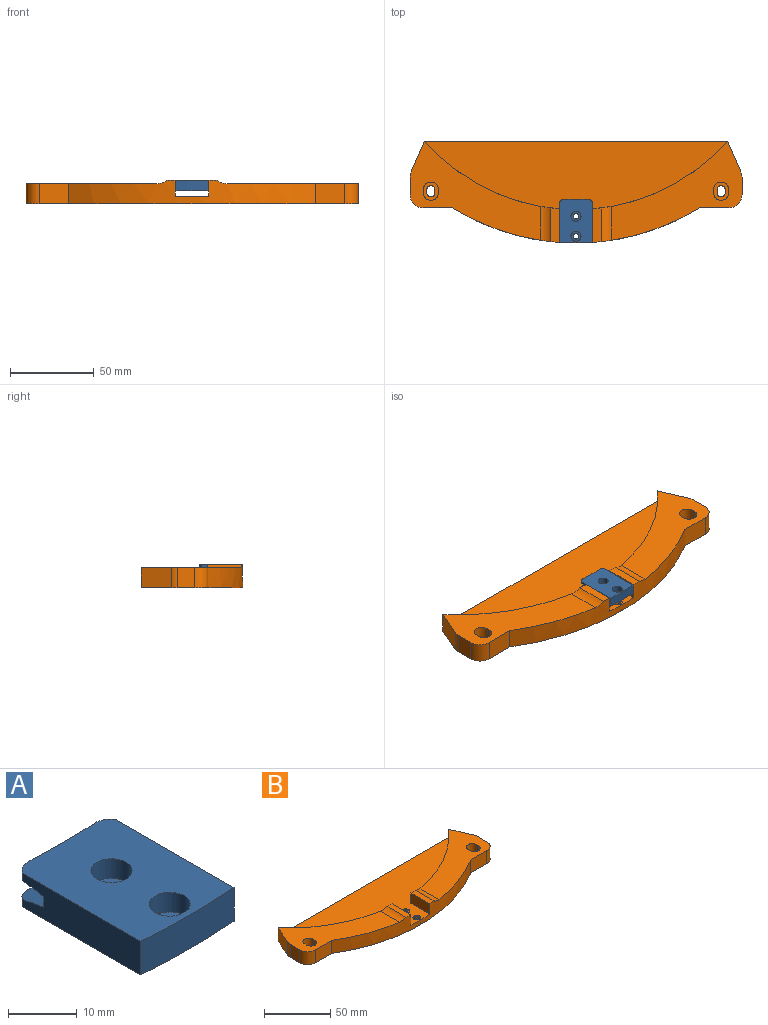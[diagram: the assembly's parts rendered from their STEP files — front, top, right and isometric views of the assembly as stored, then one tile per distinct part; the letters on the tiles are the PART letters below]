
ASSEMBLY  parts=2 mates=1
PART A: 24 faces, bbox 19.9x26.4x6 mm
  f0: cylinder r=1.7mm len=3.4mm, axis (0,0,1), area 21.4mm2, adj f10,f23
  f1: cylinder r=1.7mm len=3.4mm, axis (0,0,1), area 21.4mm2, adj f11,f21
  f2: plane 26.21x19.2mm, normal (0,0,1), area 440.4mm2, adj f7,f9,f12,f13,f14,f15,f18,f19
  f3: plane 26.21x19.2mm, normal (0,0,-1), area 440.4mm2, adj f7,f8,f16,f17,f18,f19,f20,f22
  f4: cylinder r=121mm len=19.2mm, axis (0,0,-1), area 36.1mm2, adj f5,f6,f18,f19
  f5: cone r=114.99mm half-angle=80deg, axis (0,0,1), area 114.3mm2, adj f4,f8,f16,f17,f18,f19
  f6: cone r=121mm half-angle=80deg, axis (0,0,-1), area 114.3mm2, adj f4,f9,f14,f15,f18,f19
  f7: cylinder r=141mm len=19.2mm, axis (0,0,-1), area 115.3mm2, adj f2,f3,f18,f19
  f8: cylinder r=115mm len=13.64mm, axis (0,0,-1), area 13.7mm2, adj f3,f5,f16,f17
  f9: cylinder r=115mm len=13.64mm, axis (0,0,-1), area 13.7mm2, adj f2,f6,f14,f15
  f10: plane 6x6mm, normal (0,0,1), area 19.2mm2, adj f0,f13
  f11: plane 6x6mm, normal (0,0,1), area 19.2mm2, adj f1,f12
  f12: cylinder r=3mm len=6mm, axis (0,0,1), area 66mm2, adj f2,f11
  f13: cylinder r=3mm len=6mm, axis (0,0,1), area 66mm2, adj f2,f10
  f14: cylinder r=3mm len=2.78mm, axis (0,0,-1), area 3.8mm2, adj f2,f6,f9,f18
  f15: cylinder r=3mm len=2.78mm, axis (0,0,-1), area 3.8mm2, adj f2,f6,f9,f19
  f16: cylinder r=3mm len=2.78mm, axis (0,0,-1), area 3.8mm2, adj f3,f5,f8,f18
  f17: cylinder r=3mm len=2.78mm, axis (0,0,-1), area 3.8mm2, adj f3,f5,f8,f19
  f18: plane 24.39x6.01mm, normal (1,0,0), area 134.9mm2, adj f2,f3,f4,f5,f6,f7,f14,f16
  f19: plane 24.39x6.01mm, normal (-1,0,0), area 134.9mm2, adj f2,f3,f4,f5,f6,f7,f15,f17
  f20: cylinder r=3mm len=6mm, axis (0,0,-1), area 9.4mm2, adj f3,f21
  f21: plane 6x6mm, normal (0,0,-1), area 19.2mm2, adj f1,f20
  f22: cylinder r=3mm len=6mm, axis (0,0,-1), area 9.4mm2, adj f3,f23
  f23: plane 6x6mm, normal (0,0,-1), area 19.2mm2, adj f0,f22
PART B: 84 faces, bbox 198.8x61x14 mm
  f0: plane 0.61x0.17mm, normal (0,0,-1), area 0mm2, adj f45,f70,f71
  f1: plane 0.52x0.3mm, normal (0,0,-1), area 0mm2, adj f45,f68,f70
  f2: plane 0.52x0.3mm, normal (0,0,-1), area 0mm2, adj f45,f66,f68
  f3: plane 0.61x0.17mm, normal (0,0,-1), area 0mm2, adj f45,f66,f67
  f4: plane 0.52x0.3mm, normal (0,0,-1), area 0mm2, adj f45,f69,f71
  f5: plane 0.52x0.3mm, normal (0,0,-1), area 0mm2, adj f44,f63,f65
  f6: plane 0.61x0.17mm, normal (0,0,-1), area 0mm2, adj f44,f61,f63
  f7: plane 0.52x0.3mm, normal (0,0,-1), area 0mm2, adj f44,f60,f61
  f8: plane 0.52x0.3mm, normal (0,0,-1), area 0mm2, adj f44,f60,f62
  f9: plane 0.52x0.3mm, normal (0,0,-1), area 0mm2, adj f44,f64,f65
  f10: plane 198.81x61mm, normal (0,0,-1), area 9740.1mm2, adj f16,f17,f18,f19,f20,f21,f22,f23
  f11: plane 78.4x59.43mm, normal (0,0,1), area 1845.7mm2, adj f17,f18,f19,f20,f33,f40,f41,f42
  f12: plane 78.4x59.43mm, normal (0,0,1), area 1845.7mm2, adj f20,f21,f22,f23,f34,f36,f37,f38
  f13: plane 181.56x61mm, normal (0,0,1), area 5503.4mm2, adj f16,f20,f32,f33,f34,f35,f72,f74
  f14: plane 11x9mm, normal (0,0,1), area 53.9mm2, adj f28,f29,f30,f31,f36,f37,f38,f39
  f15: plane 11x9mm, normal (0,0,1), area 53.9mm2, adj f24,f25,f26,f27,f40,f41,f42,f43
  f16: plane 181.56x4.5mm, normal (0,1,0), area 817mm2, adj f10,f13,f17,f23
  f17: plane 18.48x12mm, normal (-0.92,0.4,0), area 241.5mm2, adj f10,f11,f16,f33,f76
  f18: plane 12x10.35mm, normal (-1,0,0), area 124.2mm2, adj f10,f11,f76,f79
  f19: plane 17.37x12mm, normal (0,-1,0), area 208.4mm2, adj f10,f11,f20,f79
  f20: cylinder r=141mm len=148.07mm, axis (0,0,-1), area 1748.3mm2, adj f10,f11,f12,f13,f19,f21,f32,f35
  f21: plane 17.37x12mm, normal (0,-1,0), area 208.4mm2, adj f10,f12,f20,f78
  f22: plane 12x10.35mm, normal (1,0,0), area 124.2mm2, adj f10,f12,f77,f78
  f23: plane 18.48x12mm, normal (0.92,0.4,0), area 241.5mm2, adj f10,f12,f16,f34,f77
  f24: cylinder r=2.4mm len=4.8mm, axis (0,0,-1), area 33.9mm2, adj f10,f15,f25,f27
  f25: plane 4.5x2mm, normal (1,0,0), area 9mm2, adj f10,f15,f24,f26
  f26: cylinder r=2.4mm len=4.8mm, axis (0,0,-1), area 33.9mm2, adj f10,f15,f25,f27
  f27: plane 4.5x2mm, normal (-1,0,0), area 9mm2, adj f10,f15,f24,f26
  f28: plane 4.5x2mm, normal (-1,0,0), area 9mm2, adj f10,f14,f29,f31
  f29: cylinder r=2.4mm len=4.8mm, axis (0,0,-1), area 33.9mm2, adj f10,f14,f28,f30
  f30: plane 4.5x2mm, normal (1,0,0), area 9mm2, adj f10,f14,f29,f31
  f31: cylinder r=2.4mm len=4.8mm, axis (0,0,-1), area 33.9mm2, adj f10,f14,f28,f30
  f32: plane 20.06x9.5mm, normal (1,0,0), area 190.6mm2, adj f13,f20,f33,f80
  f33: cylinder r=121mm len=80.78mm, axis (0,0,-1), area 708.8mm2, adj f11,f13,f17,f32,f80,f83
  f34: cylinder r=121mm len=80.78mm, axis (0,0,-1), area 708.8mm2, adj f12,f13,f23,f35,f81,f82
  f35: plane 20.06x9.5mm, normal (-1,0,0), area 190.6mm2, adj f13,f20,f34,f81
  f36: cylinder r=4.5mm len=9mm, axis (0,0,-1), area 106mm2, adj f12,f14,f37,f39
  f37: plane 7.5x2mm, normal (1,0,0), area 15mm2, adj f12,f14,f36,f38
  f38: cylinder r=4.5mm len=9mm, axis (0,0,-1), area 106mm2, adj f12,f14,f37,f39
  f39: plane 7.5x2mm, normal (-1,0,0), area 15mm2, adj f12,f14,f36,f38
  f40: plane 7.5x2mm, normal (1,0,0), area 15mm2, adj f11,f15,f41,f43
  f41: cylinder r=4.5mm len=9mm, axis (0,0,-1), area 106mm2, adj f11,f15,f40,f42
  f42: plane 7.5x2mm, normal (-1,0,0), area 15mm2, adj f11,f15,f41,f43
  f43: cylinder r=4.5mm len=9mm, axis (0,0,-1), area 106mm2, adj f11,f15,f40,f42
  f44: cylinder r=1.7mm len=3.4mm, axis (0,0,1), area 11mm2, adj f5,f6,f7,f8,f9,f53,f60,f61
  f45: cylinder r=1.7mm len=3.4mm, axis (0,0,1), area 11mm2, adj f0,f1,f2,f3,f4,f46,f66,f67
  f46: plane 0.52x0.3mm, normal (0,0,-1), area 0mm2, adj f45,f67,f69
  f47: plane 3x2mm, normal (0.5,0.87,0), area 6.9mm2, adj f10,f48,f52,f66
  f48: plane 3x2mm, normal (-0.5,0.87,0), area 6.9mm2, adj f10,f47,f49,f67
  f49: plane 3.46x2mm, normal (-1,0,0), area 6.9mm2, adj f10,f48,f50,f69
  f50: plane 3x2mm, normal (-0.5,-0.87,0), area 6.9mm2, adj f10,f49,f51,f71
  f51: plane 3x2mm, normal (0.5,-0.87,0), area 6.9mm2, adj f10,f50,f52,f70
  f52: plane 3.46x2mm, normal (1,0,0), area 6.9mm2, adj f10,f47,f51,f68
  f53: plane 0.61x0.17mm, normal (0,0,-1), area 0mm2, adj f44,f62,f64
  f54: plane 3x2mm, normal (-0.5,-0.87,0), area 6.9mm2, adj f10,f55,f58,f62
  f55: plane 3x2mm, normal (0.5,-0.87,0), area 6.9mm2, adj f10,f54,f56,f64
  f56: plane 3.46x2mm, normal (1,0,0), area 6.9mm2, adj f10,f55,f57,f65
  f57: plane 3x2mm, normal (0.5,0.87,0), area 6.9mm2, adj f10,f56,f59,f63
  f58: plane 3.46x2mm, normal (-1,0,0), area 6.9mm2, adj f10,f54,f59,f60
  f59: plane 3x2mm, normal (-0.5,0.87,0), area 6.9mm2, adj f10,f57,f58,f61
  f60: plane 3.5x1.44mm, normal (-0.58,0,-0.81), area 4.5mm2, adj f7,f8,f44,f58,f61,f62
  f61: plane 3x2.54mm, normal (-0.29,0.5,-0.81), area 4.5mm2, adj f6,f7,f44,f59,f60,f63
  f62: plane 3x2.54mm, normal (-0.29,-0.5,-0.81), area 4.5mm2, adj f8,f44,f53,f54,f60,f64
  f63: plane 3x2.54mm, normal (0.29,0.5,-0.81), area 4.5mm2, adj f5,f6,f44,f57,f61,f65
  f64: plane 3x2.54mm, normal (0.29,-0.5,-0.81), area 4.5mm2, adj f9,f44,f53,f55,f62,f65
  f65: plane 3.46x1.4mm, normal (0.58,0,-0.81), area 4.5mm2, adj f5,f9,f44,f56,f63,f64
  f66: plane 3x2.54mm, normal (0.29,0.5,-0.81), area 4.5mm2, adj f2,f3,f45,f47,f67,f68
  f67: plane 3x2.54mm, normal (-0.29,0.5,-0.81), area 4.5mm2, adj f3,f45,f46,f48,f66,f69
  f68: plane 3.46x1.4mm, normal (0.58,0,-0.81), area 4.5mm2, adj f1,f2,f45,f52,f66,f70
  f69: plane 3.5x1.44mm, normal (-0.58,0,-0.81), area 4.5mm2, adj f4,f45,f46,f49,f67,f71
  f70: plane 3x2.54mm, normal (0.29,-0.5,-0.81), area 4.5mm2, adj f0,f1,f45,f51,f68,f71
  f71: plane 3x2.54mm, normal (-0.29,-0.5,-0.81), area 4.5mm2, adj f0,f4,f45,f50,f69,f70
  f72: cylinder r=3mm len=6mm, axis (0,0,-1), area 9.4mm2, adj f13,f73
  f73: plane 6x6mm, normal (0,0,1), area 19.2mm2, adj f45,f72
  f74: cylinder r=3mm len=6mm, axis (0,0,-1), area 9.4mm2, adj f13,f75
  f75: plane 6x6mm, normal (0,0,1), area 19.2mm2, adj f44,f74
  f76: cylinder r=8mm len=12mm, axis (0,0,-1), area 39.1mm2, adj f10,f11,f17,f18
  f77: cylinder r=8mm len=12mm, axis (0,0,-1), area 39.1mm2, adj f10,f12,f22,f23
  f78: cylinder r=8mm len=12mm, axis (0,0,-1), area 150.8mm2, adj f10,f12,f21,f22
  f79: cylinder r=8mm len=12mm, axis (0,0,-1), area 150.8mm2, adj f10,f11,f18,f19
  f80: plane 20.58x5mm, normal (0,0,1), area 100.5mm2, adj f20,f32,f33,f83
  f81: plane 20.58x5mm, normal (0,0,1), area 100.5mm2, adj f20,f34,f35,f82
  f82: cylinder r=10mm len=21.04mm, axis (0,-1,0), area 129.9mm2, adj f12,f20,f34,f81
  f83: cylinder r=10mm len=21.04mm, axis (0,-1,0), area 129.9mm2, adj f11,f20,f33,f80
PLACE A t=(0,0.03,2.81)mm
PLACE B at identity fixed
MATE slider B.f13 <-> A.f3  axis (0,0,1) through (-10,-140.64,4.5)mm
